# Revit family: Vitra-Plural-Shelf-64062
name_source: partatom
category: Furniture Systems
revit_build: Autodesk Revit 2017 (Build: 20160225_1515(x64)
units: mm (PartAtom-declared; Revit-internal decimal feet)

## family parameters
Cut with Voids When Loaded = No
Host = Face
OmniClass Number = 23.40.00.00
OmniClass Title = Equipment and Furnishings
Part Type = Normal
Room Calculation Point = No
Round Connector Dimension = Use Diameter
Shared = Yes

## types (1)
- WashbasinUnit-Vitra-Plural-LongShelf(AmericanValnut)_64062
    Article No. (default) = 64062
    BIMobject category = Storage
    Color = American Valnut
    Construction Type = Face Mounted
    Default Elevation = 1200 mm
    Depth(mm) = 180 mm  [stored 0.590551 ft]
    Description = Plural Shelves
    Design country = Turkey
    Height(mm) = 100 mm  [stored 0.328084 ft]
    IFC Classification = Sanitary Terminal
    Manufacturer = Vitra
    Manufacturer name = Vitra
    Model = 64062
    NBS Referans Code = 35-77-80
    Nominal height = 0.000
    Nominal width = 0.000
    OmniClass Code = 23-21 11 11 11
    OmniClass Description = Commercial Storage Shelves
    Primary Material = Vitra-AmericanValnut
    Product SKU = 64062
    Product certification = https://vitraglobal.com
    Product data url = https://www.vitra.com.tr
    Product family = Plural
    Product group = Shelves
    Secondary Material = Vitra-DarkOlive
    Technical description = https://www.vitra.com.tr
    Thrid Material = Vitra-AmericanValnut
    URL = https://vitraglobal.com
    Uniclass 1.4 Code = L8261
    Uniclass 1.4 Description = Shelves
    Uniclass 2.0 Code = PR-35-77-80
    Uniclass 2.0 Description = Shelves
    Uniclass 2015 Code = Pr_40_30_78_78
    Uniclass 2015 Name = Shelves
    Warranty Period (Year) = 2
    Weight Net (kg) = 3,200
    Width(mm) = 750 mm
    Youtube = https://www.youtube.com

note: [stored X ft] marks values corroborated as IEEE doubles in the binary element streams (Revit-internal decimal feet)

## geometry (parser evidence)
native form markers: Sweep x3
no freeform markers — native parametric forms only
